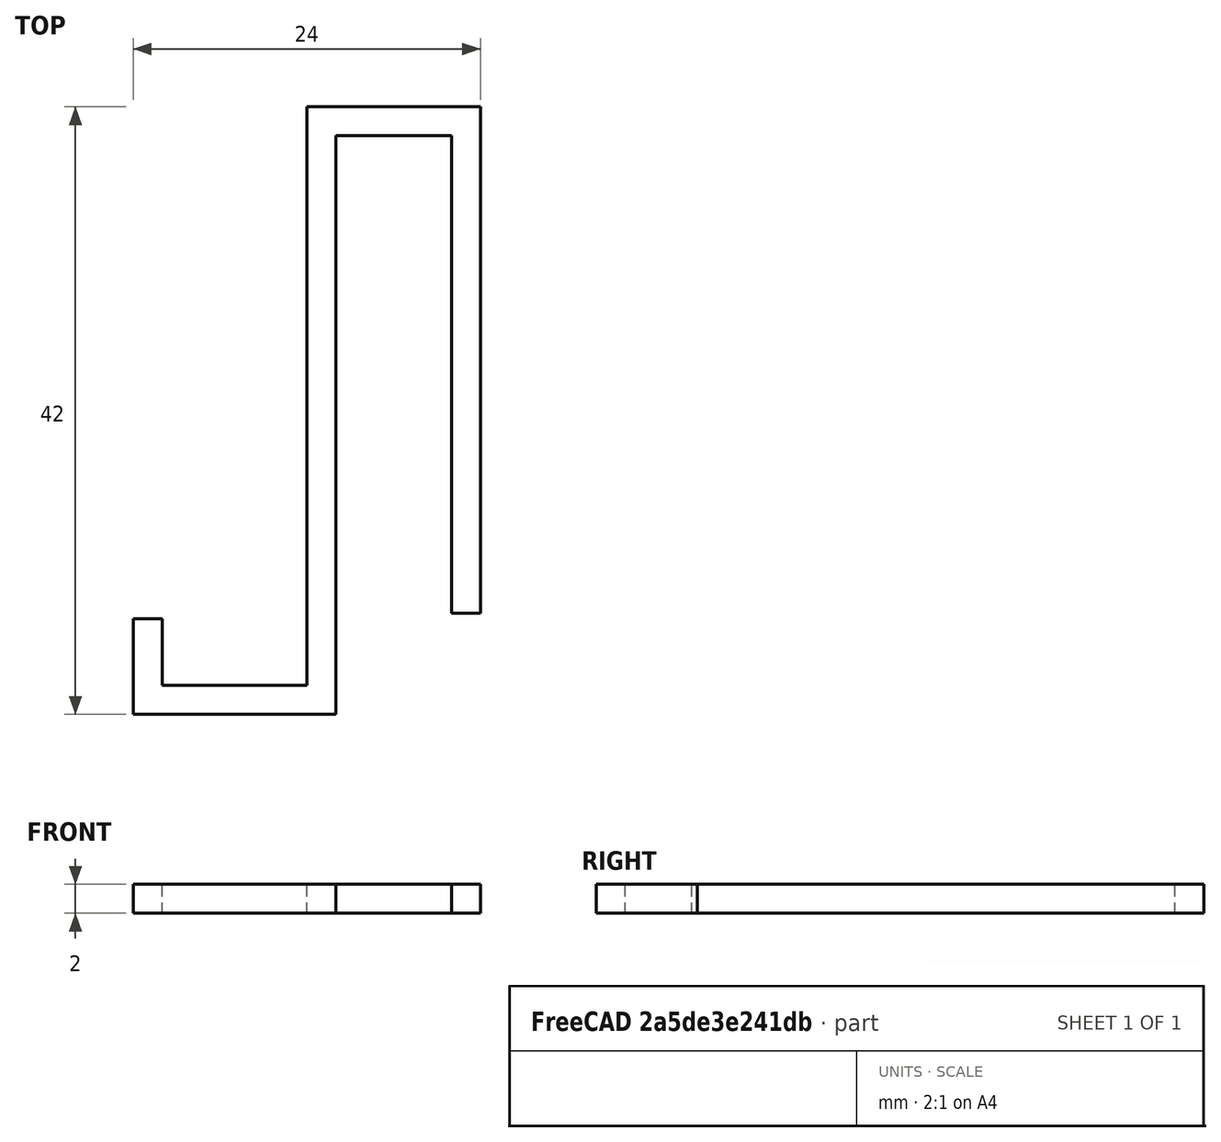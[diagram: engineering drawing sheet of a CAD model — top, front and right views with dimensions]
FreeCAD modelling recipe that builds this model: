
FCSTD DOCUMENT  (FreeCAD 0.21R33694 (Git))
Label: 7mmTankHook
License: All rights reserved
LicenseURL: https://en.wikipedia.org/wiki/All_rights_reserved
objects: PartDesign::Body×2, Sketcher::SketchObject×1, PartDesign::Pad×1
note: 5 computed .brp shape members not serialized (recipe doc carries the construction recipe); baked Part::Feature solids carry a one-line shape summary decoded from their .brp

FEATURE [PartDesign::Body] Body
  Origin = -> Origin
FEATURE [Sketcher::SketchObject] Sketch
  FullyConstrained = false
  MapMode = 5
  Support = -> [XY_Plane001]
  sketch-geometry (12):
    g0: LineSegment StartX=0 StartY=0 StartZ=0 EndX=-2 EndY=0 EndZ=0
    g1: LineSegment StartX=-2 StartY=0 StartZ=0 EndX=-2 EndY=-6.59805 EndZ=0
    g2: LineSegment StartX=-2 StartY=-6.59805 StartZ=0 EndX=12 EndY=-6.59805 EndZ=0
    g3: LineSegment StartX=12 StartY=-6.59805 StartZ=0 EndX=12 EndY=33.4019 EndZ=0
    g4: LineSegment StartX=12 StartY=33.4019 StartZ=0 EndX=20 EndY=33.4019 EndZ=0
    g5: LineSegment StartX=20 StartY=33.4019 StartZ=0 EndX=20 EndY=0.401946 EndZ=0
    g6: LineSegment StartX=20 StartY=0.401946 StartZ=0 EndX=22 EndY=0.401946 EndZ=0
    g7: LineSegment StartX=22 StartY=0.401946 StartZ=0 EndX=22 EndY=35.4019 EndZ=0
    g8: LineSegment StartX=22 StartY=35.4019 StartZ=0 EndX=10 EndY=35.4019 EndZ=0
    g9: LineSegment StartX=10 StartY=35.4019 StartZ=0 EndX=10 EndY=-4.59805 EndZ=0
    g10: LineSegment StartX=10 StartY=-4.59805 StartZ=0 EndX=0 EndY=-4.59805 EndZ=0
    g11: LineSegment StartX=0 StartY=-4.59805 StartZ=0 EndX=0 EndY=0 EndZ=0
  constraints (34):
    c: Coincident(g-1,g0)
    c: PointOnObject(g0,g-1)
    c: Coincident(g0,g1)
    c: Vertical(g1)
    c: Coincident(g1,g2)
    c: Horizontal(g2)
    c: Coincident(g2,g3)
    c: Vertical(g3)
    c: Coincident(g3,g4)
    c: Horizontal(g4)
    c: Coincident(g4,g5)
    c: Vertical(g5)
    c: Coincident(g5,g6)
    c: Coincident(g6,g7)
    c: Vertical(g7)
    c: Coincident(g7,g8)
    c: Coincident(g8,g9)
    c: Vertical(g9)
    c: Coincident(g9,g10)
    c: Horizontal(g10)
    c: Coincident(g10,g11)
    c: Coincident(g11,g0)
    c: DistanceX(g0,g0) = 2
    c: DistanceX(g6,g6) = 2
    c: DistanceY(g6,g5) = 0
    c: DistanceY(g7,g8) = 0
    c: DistanceX(g10,g0) = 0
    c: DistanceX(g8,g3) = 2
    c: DistanceY(g4,g7) = 2
    c: DistanceX(g4,g4) = 8
    c: DistanceY(g1,g10) = 2
    c: DistanceX(g10,g10) = 10
    c: DistanceY(g9,g9) = 40
    c: DistanceY(g7,g7) = 35
FEATURE [PartDesign::Pad] Pad
  Direction = (0,0,1)
  Length = 2
  Length2 = 10
  Profile = -> Sketch
  ReferenceAxis = -> Sketch [N_Axis]
  Type = 0
FEATURE [PartDesign::Body] Body001
  Group = -> [Sketch,Pad]
  Origin = -> Origin001
  Tip = -> Pad
